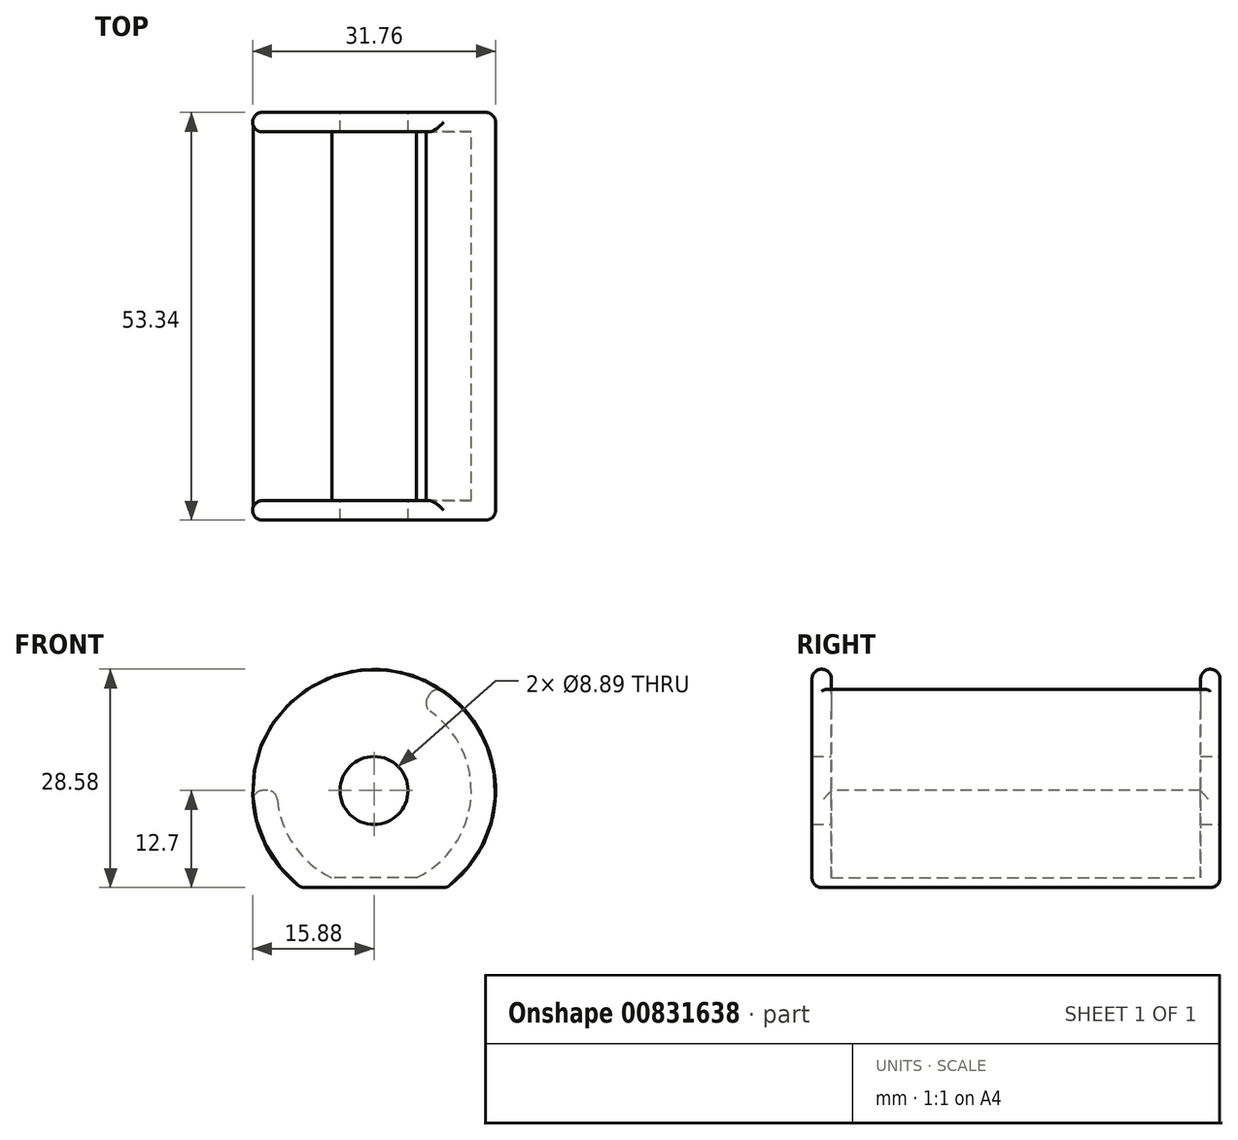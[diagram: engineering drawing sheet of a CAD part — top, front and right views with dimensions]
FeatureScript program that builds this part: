
annotation { "Feature Type Name" : "Feature", "Feature Type Description" : "" }
export const myFeature = defineFeature(function(context is Context, id is Id, definition is map)
    precondition{}
    {
        {
            var Q0;
            Q0=qCreatedBy(makeId("Front.planeOp"),FACE);
            var sketch = newSketch(context, id + "F0", { "sketchPlane" : qUnion([Q0])});
            skLineSegment(sketch, "E0", {"start": v(-9.53, 0) * mm, "end": v(9.53, 0) * mm});
            skPoint(sketch, "E1", {"position": v(0, 0) * mm});
            skArc(sketch, "E2", {"start": v(9.53, 0) * mm, "mid": v(0, 28.58) * mm, "end": v(-9.53, 0) * mm});
            skLineSegment(sketch, "E3", {"start": v(0, 0) * mm, "end": v(0, 0) * mm});
            skCircle(sketch, "E4", {"center": v(0, 12.7) * mm, "radius": 4.45 * mm});
            skLineSegment(sketch, "E5", {"start": v(7.94, 26.45) * mm, "end": v(6.35, 23.7) * mm});
            skLineSegment(sketch, "E6", {"start": v(7.94, 26.45) * mm, "end": v(-7.33, 0) * mm, "construction": true});
            skLineSegment(sketch, "E7", {"start": v(5.54, 1.27) * mm, "end": v(-5.54, 1.27) * mm});
            skLineSegment(sketch, "E8", {"start": v(-12.7, 12.7) * mm, "end": v(-15.88, 12.7) * mm});
            skArc(sketch, "E9", {"start": v(5.54, 1.27) * mm, "mid": v(0, 25.4) * mm, "end": v(-5.54, 1.27) * mm});
            skSolve(sketch);
        }
        {
            var Q0;
            {var subQ0=sQuery(id+"F0.wireOp",EDGE,"E5");Q0=makeQuery(id+"F0.imprint","IMPRINT",FACE,{"disambiguationData":[TD([[makeQuery(id+"F0.imprint","IMPRINT",EDGE,{"derivedFrom":subQ0}),-1.0]])]});}
            var Q1;
            Q1=makeQuery(id+"F0.imprint","IMPRINT",FACE,{"disambiguationData":[TD([[makeQuery(id+"F0.imprint","IMPRINT",EDGE,{"derivedFrom":sQuery(id+"F0.wireOp",EDGE,"E4")}),-1.0]])]});
            extrude(context, id + "F1", {"entities" : qUnion([Q0, Q1]), "depth" : 2.54 * mm, "offsetDistance" : 25.4 * mm});
        }
        {
            var Q0;
            {var subQ2=sQuery(id+"F0.wireOp",EDGE,"E8");Q0=makeQuery(id+"F0.imprint","IMPRINT",FACE,{"disambiguationData":[TD([[makeQuery(id+"F0.imprint","IMPRINT",EDGE,{"derivedFrom":subQ2}),1.0]])]});}
            var Q1;
            {var subQ4=sQuery(id+"F0.wireOp",EDGE,"E7");Q1=makeQuery(id+"F0.imprint","IMPRINT",FACE,{"disambiguationData":[TD([[makeQuery(id+"F0.imprint","IMPRINT",EDGE,{"derivedFrom":subQ4}),1.0]])]});}
            var Q2;
            {var subQ6=sQuery(id+"F0.wireOp",EDGE,"E5");Q2=makeQuery(id+"F0.imprint","IMPRINT",FACE,{"disambiguationData":[TD([[makeQuery(id+"F0.imprint","IMPRINT",EDGE,{"derivedFrom":subQ6}),1.0]])]});}
            extrude(context, id + "F2", {"entities" : qUnion([Q0, Q1, Q2]), "operationType" : NewBodyOperationType.ADD, "depth" : 50.8 * mm, "offsetDistance" : 25.4 * mm});
        }
        {
            var Q0;
            Q0=makeQuery(id+"F2.opExtrude","CAP_FACE",FACE,{"disambiguationData":[OSD([sQuery(id+"F0.wireOp",EDGE,"E0"),sQuery(id+"F0.wireOp",EDGE,"E2"),sQuery(id+"F0.wireOp",EDGE,"E5"),sQuery(id+"F0.wireOp",EDGE,"E7"),sQuery(id+"F0.wireOp",EDGE,"E8"),sQuery(id+"F0.wireOp",EDGE,"E9")])],"isStart":false});
            var sketch = newSketch(context, id + "F3", { "sketchPlane" : qUnion([Q0])});
            skCircle(sketch, "E10.0", {"center": v(0, 12.7) * mm, "radius": 4.45 * mm});
            skArc(sketch, "E11.0", {"start": v(7.94, 26.45) * mm, "mid": v(-7.94, 26.45) * mm, "end": v(-15.88, 12.7) * mm});
            skArc(sketch, "E11.1", {"start": v(-15.88, 12.7) * mm, "mid": v(-14.2, 5.6) * mm, "end": v(-9.52, 0) * mm});
            skLineSegment(sketch, "E11.2", {"start": v(-9.53, 0) * mm, "end": v(9.53, 0) * mm});
            skArc(sketch, "E11.3", {"start": v(9.52, 0) * mm, "mid": v(15.85, 13.65) * mm, "end": v(7.94, 26.45) * mm});
            skArc(sketch, "E12.0", {"start": v(-12.7, 12.7) * mm, "mid": v(-10.76, 5.96) * mm, "end": v(-5.54, 1.27) * mm});
            skCircle(sketch, "E13", {"center": v(0, 12.7) * mm, "radius": 12.7 * mm});
            skSolve(sketch);
        }
        {
            var Q0;
            Q0=makeQuery(id+"F3.imprint","IMPRINT",FACE,{"disambiguationData":[TD([[makeQuery(id+"F3.imprint","IMPRINT",EDGE,{"derivedFrom":sQuery(id+"F3.wireOp",EDGE,"E10.0")}),-1.0]])]});
            var Q1;
            {var subQ5=sQuery(id+"F3.wireOp",EDGE,"E11.1");Q1=makeQuery(id+"F3.imprint","IMPRINT",FACE,{"disambiguationData":[TD([[makeQuery(id+"F3.imprint","IMPRINT",EDGE,{"derivedFrom":subQ5}),1.0]])]});}
            var Q2;
            {var subQ5=sQuery(id+"F3.wireOp",EDGE,"E11.3");Q2=makeQuery(id+"F3.imprint","IMPRINT",FACE,{"disambiguationData":[TD([[makeQuery(id+"F3.imprint","IMPRINT",EDGE,{"derivedFrom":subQ5}),1.0]])]});}
            var Q3;
            {var subQ1=makeQuery(id+"F2.opExtrude","CAP_EDGE",EDGE,{"disambiguationData":[OSD([sQuery(id+"F0.wireOp",EDGE,"E7")])],"isStart":false});Q3=makeQuery(id+"F3.imprint","IMPRINT",FACE,{"disambiguationData":[TD([[makeQuery(id+"F3.imprint","IMPRINT",EDGE,{"derivedFrom":subQ1}),1.0]])]});}
            var Q4;
            Q4=makeQuery(id+"F3.imprint","IMPRINT",FACE,{"disambiguationData":[TD([[makeQuery(id+"F3.imprint","IMPRINT",EDGE,{"derivedFrom":sQuery(id+"F3.wireOp",EDGE,"E11.0")}),1.0]])]});
            extrude(context, id + "F4", {"entities" : qUnion([Q0, Q1, Q2, Q3, Q4]), "operationType" : NewBodyOperationType.ADD, "depth" : 2.54 * mm, "offsetDistance" : 25.4 * mm});
        }
        {
            var Q0;
            Q0=makeQuery(id+"F2.opExtrude","SWEPT_EDGE",EDGE,{"disambiguationData":[OSD([sQuery(id+"F0.wireOp",EDGE,"E2"),sQuery(id+"F0.wireOp",EDGE,"E8")])]});
            var Q1;
            Q1=makeQuery(id+"F2.opExtrude","SWEPT_EDGE",EDGE,{"disambiguationData":[OSD([sQuery(id+"F0.wireOp",EDGE,"E8"),sQuery(id+"F0.wireOp",EDGE,"E9")])]});
            var Q2;
            Q2=makeQuery(id+"F2.opExtrude","SWEPT_EDGE",EDGE,{"disambiguationData":[OSD([sQuery(id+"F0.wireOp",EDGE,"E5"),sQuery(id+"F0.wireOp",EDGE,"E9")])]});
            var Q3;
            Q3=makeQuery(id+"F2.opExtrude","SWEPT_EDGE",EDGE,{"disambiguationData":[OSD([sQuery(id+"F0.wireOp",EDGE,"E2"),sQuery(id+"F0.wireOp",EDGE,"E5")])]});
            var Q4;
            Q4=makeQuery(id+"F1.opExtrude","CAP_EDGE",EDGE,{"disambiguationData":[OSD([sQuery(id+"F0.wireOp",EDGE,"E2")])],"isStart":false});
            var Q5;
            {var subQ0=sQuery(id+"F0.wireOp",EDGE,"E2");var subQ1=sQuery(id+"F0.wireOp",EDGE,"E0");Q5=makeQuery(id+"F2.boolean.opBoolean","MERGE",EDGE,{"derivedFrom":[makeQuery(id+"F1.opExtrude","CAP_EDGE",EDGE,{"disambiguationData":[OSD([subQ0])],"isStart":true}),makeQuery(id+"F2.opExtrude","CAP_EDGE",EDGE,{"disambiguationData":[OSD([subQ0]),TDD([makeQuery(id+"F0.imprint","IMPRINT",EDGE,{"disambiguationData":[TD([[makeQuery(id+"F0.imprint","INTERSECT",VERTEX,{"disambiguationData":[OD(1.0)],"derivedFrom":[subQ1,subQ0]}),-1.0]])],"derivedFrom":subQ0})])],"isStart":true}),makeQuery(id+"F2.opExtrude","CAP_EDGE",EDGE,{"disambiguationData":[OSD([subQ0]),TDD([makeQuery(id+"F0.imprint","IMPRINT",EDGE,{"disambiguationData":[TD([[makeQuery(id+"F0.imprint","INTERSECT",VERTEX,{"disambiguationData":[OD(0.0)],"derivedFrom":[subQ1,subQ0]}),1.0]])],"derivedFrom":subQ0})])],"isStart":true})]});}
            var Q6;
            Q6=makeQuery(id+"F4.opExtrude","CAP_EDGE",EDGE,{"disambiguationData":[OSD([sQuery(id+"F3.wireOp",EDGE,"E11.0"),sQuery(id+"F3.wireOp",EDGE,"E11.1"),sQuery(id+"F3.wireOp",EDGE,"E11.3")])],"isStart":false});
            var Q7;
            Q7=makeQuery(id+"F4.opExtrude","CAP_EDGE",EDGE,{"disambiguationData":[OSD([sQuery(id+"F3.wireOp",EDGE,"E11.0"),sQuery(id+"F3.wireOp",EDGE,"E11.1"),sQuery(id+"F3.wireOp",EDGE,"E11.3")])],"isStart":true});
            var Q8;
            {var subQ0=sQuery(id+"F0.wireOp",EDGE,"E2");var subQ1=sQuery(id+"F0.wireOp",EDGE,"E0");Q8=makeQuery(id+"F4.boolean.opBoolean","MERGE",EDGE,{"derivedFrom":[makeQuery(id+"F2.opExtrude","SWEPT_EDGE",EDGE,{"disambiguationData":[OSD([subQ1,subQ0]),TDD([makeQuery(id+"F0.imprint","INTERSECT",VERTEX,{"disambiguationData":[OD(0.0)],"derivedFrom":[subQ1,subQ0]})])]}),makeQuery(id+"F4.opExtrude","SWEPT_EDGE",EDGE,{"disambiguationData":[OSD([sQuery(id+"F3.wireOp",EDGE,"E11.1"),sQuery(id+"F3.wireOp",EDGE,"E11.2")])]})]});}
            var Q9;
            {var subQ0=sQuery(id+"F0.wireOp",EDGE,"E2");var subQ1=sQuery(id+"F0.wireOp",EDGE,"E0");Q9=makeQuery(id+"F4.boolean.opBoolean","MERGE",EDGE,{"derivedFrom":[makeQuery(id+"F2.opExtrude","SWEPT_EDGE",EDGE,{"disambiguationData":[OSD([subQ1,subQ0]),TDD([makeQuery(id+"F0.imprint","INTERSECT",VERTEX,{"disambiguationData":[OD(1.0)],"derivedFrom":[subQ1,subQ0]})])]}),makeQuery(id+"F4.opExtrude","SWEPT_EDGE",EDGE,{"disambiguationData":[OSD([sQuery(id+"F3.wireOp",EDGE,"E11.2"),sQuery(id+"F3.wireOp",EDGE,"E11.3")])]})]});}
            var Q10;
            Q10=makeQuery(id+"F4.opExtrude","CAP_EDGE",EDGE,{"disambiguationData":[OSD([sQuery(id+"F3.wireOp",EDGE,"E11.2")])],"isStart":false});
            var Q11;
            Q11=makeQuery(id+"F2.opExtrude","CAP_EDGE",EDGE,{"disambiguationData":[OSD([sQuery(id+"F0.wireOp",EDGE,"E0")])],"isStart":true});
            fillet(context, id + "F5", {"entities" : qUnion([Q0, Q1, Q2, Q3, Q4, Q5, Q6, Q7, Q8, Q9, Q10, Q11]), "radius" : 1.27 * mm, "tangentPropagation" : true, "allowEdgeOverflow" : false});
        }
    });
